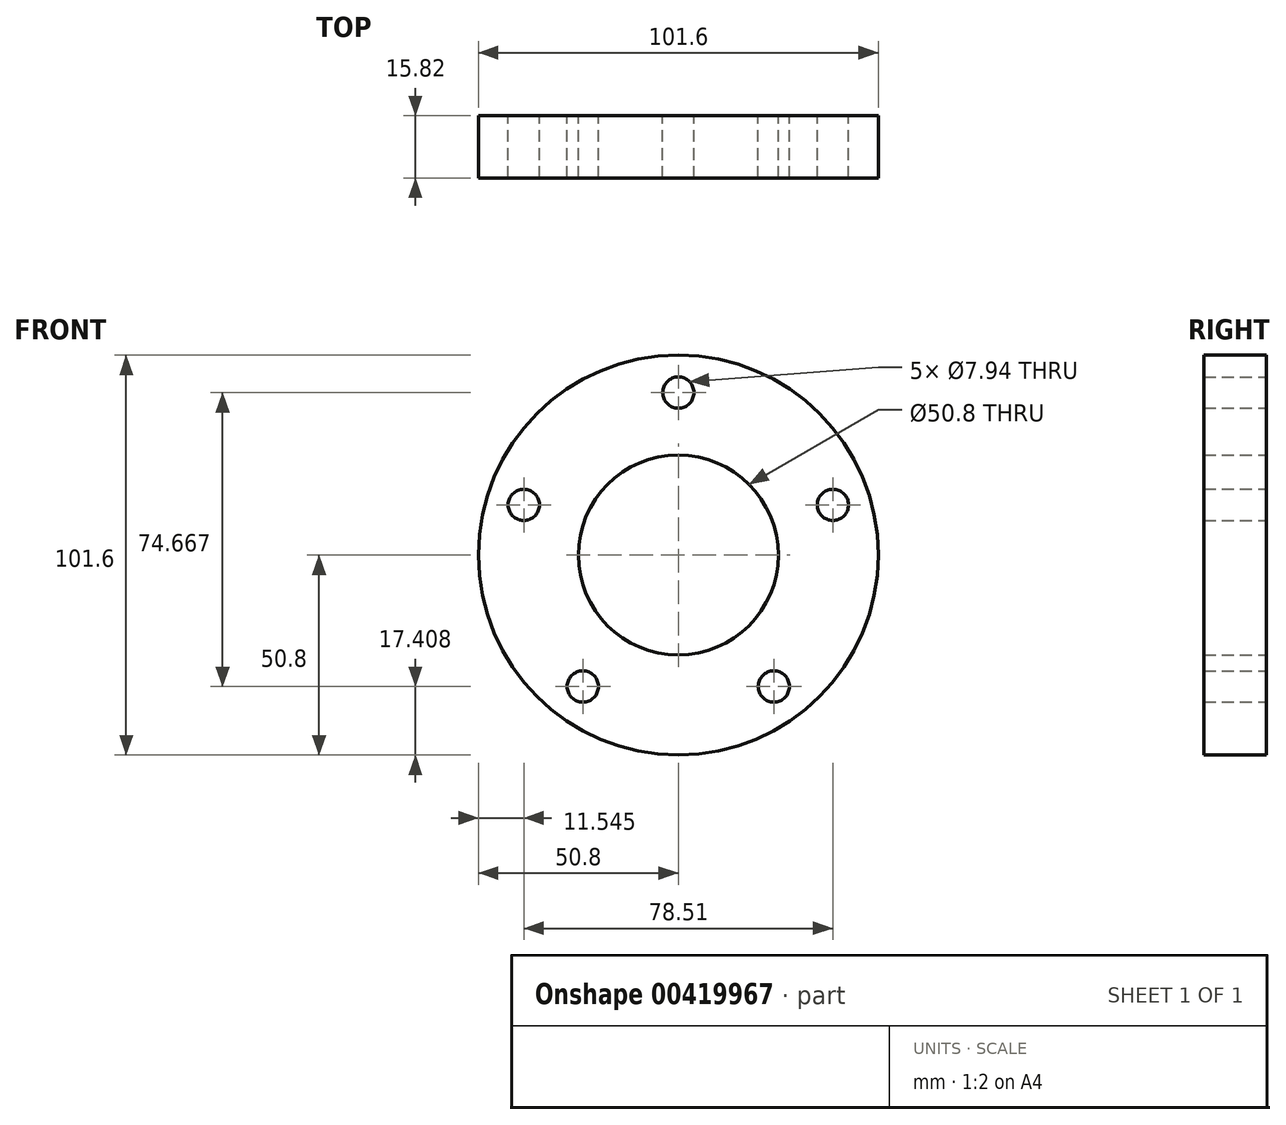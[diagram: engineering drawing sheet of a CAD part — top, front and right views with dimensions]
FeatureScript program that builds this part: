
annotation { "Feature Type Name" : "Feature", "Feature Type Description" : "" }
export const myFeature = defineFeature(function(context is Context, id is Id, definition is map)
    precondition{}
    {
        {
            var Q0;
            Q0=qCreatedBy(makeId("Front.planeOp"),FACE);
            var sketch = newSketch(context, id + "F0", { "sketchPlane" : qUnion([Q0])});
            skCircle(sketch, "E0", {"center": v(0, 0) * mm, "radius": 25.4 * mm});
            skCircle(sketch, "E1", {"center": v(0, 0) * mm, "radius": 50.8 * mm});
            skCircle(sketch, "E2", {"center": v(0, 0) * mm, "radius": 41.28 * mm});
            skLineSegment(sketch, "E3", {"start": v(0, 41.28) * mm, "end": v(0, 0) * mm});
            skLineSegment(sketch, "E4", {"start": v(0, 0) * mm, "end": v(39.25, 12.75) * mm});
            skLineSegment(sketch, "E5", {"start": v(0, 0) * mm, "end": v(24.26, -33.4) * mm});
            skLineSegment(sketch, "E6", {"start": v(0, 0) * mm, "end": v(-24.26, -33.4) * mm});
            skLineSegment(sketch, "E7", {"start": v(0, 0) * mm, "end": v(-39.25, 12.75) * mm});
            skPoint(sketch, "E8", {"position": v(0, 41.28) * mm});
            skPoint(sketch, "E9", {"position": v(-39.25, 12.75) * mm});
            skPoint(sketch, "E10", {"position": v(-24.26, -33.4) * mm});
            skPoint(sketch, "E11", {"position": v(24.26, -33.4) * mm});
            skPoint(sketch, "E12", {"position": v(39.25, 12.75) * mm});
            skSolve(sketch);
        }
        {
            var Q0;
            {var subQ0=sQuery(id+"F0.wireOp",EDGE,"E3");var subQ1=sQuery(id+"F0.wireOp",EDGE,"E0");var subQ2=makeQuery(id+"F0.imprint","INTERSECT",VERTEX,{"derivedFrom":[subQ1,subQ0]});Q0=makeQuery(id+"F0.imprint","IMPRINT",FACE,{"disambiguationData":[TD([[makeQuery(id+"F0.imprint","IMPRINT",EDGE,{"disambiguationData":[TD([[subQ2,1.0]])],"derivedFrom":subQ1}),-1.0]])]});}
            var Q1;
            Q1=makeQuery(id+"F0.imprint","IMPRINT",FACE,{"disambiguationData":[TD([[makeQuery(id+"F0.imprint","IMPRINT",EDGE,{"derivedFrom":sQuery(id+"F0.wireOp",EDGE,"E1")}),1.0]])]});
            var Q2;
            {var subQ0=sQuery(id+"F0.wireOp",EDGE,"E3");var subQ1=sQuery(id+"F0.wireOp",EDGE,"E0");var subQ2=makeQuery(id+"F0.imprint","INTERSECT",VERTEX,{"derivedFrom":[subQ1,subQ0]});Q2=makeQuery(id+"F0.imprint","IMPRINT",FACE,{"disambiguationData":[TD([[makeQuery(id+"F0.imprint","IMPRINT",EDGE,{"disambiguationData":[TD([[subQ2,-1.0]])],"derivedFrom":subQ1}),-1.0]])]});}
            var Q3;
            {var subQ0=sQuery(id+"F0.wireOp",EDGE,"E7");var subQ1=sQuery(id+"F0.wireOp",EDGE,"E0");var subQ2=makeQuery(id+"F0.imprint","INTERSECT",VERTEX,{"derivedFrom":[subQ1,subQ0]});Q3=makeQuery(id+"F0.imprint","IMPRINT",FACE,{"disambiguationData":[TD([[makeQuery(id+"F0.imprint","IMPRINT",EDGE,{"disambiguationData":[TD([[subQ2,-1.0]])],"derivedFrom":subQ1}),-1.0]])]});}
            var Q4;
            {var subQ0=sQuery(id+"F0.wireOp",EDGE,"E4");var subQ1=sQuery(id+"F0.wireOp",EDGE,"E0");var subQ2=makeQuery(id+"F0.imprint","INTERSECT",VERTEX,{"derivedFrom":[subQ1,subQ0]});Q4=makeQuery(id+"F0.imprint","IMPRINT",FACE,{"disambiguationData":[TD([[makeQuery(id+"F0.imprint","IMPRINT",EDGE,{"disambiguationData":[TD([[subQ2,1.0]])],"derivedFrom":subQ1}),-1.0]])]});}
            var Q5;
            {var subQ0=sQuery(id+"F0.wireOp",EDGE,"E6");var subQ1=sQuery(id+"F0.wireOp",EDGE,"E0");var subQ2=makeQuery(id+"F0.imprint","INTERSECT",VERTEX,{"derivedFrom":[subQ1,subQ0]});Q5=makeQuery(id+"F0.imprint","IMPRINT",FACE,{"disambiguationData":[TD([[makeQuery(id+"F0.imprint","IMPRINT",EDGE,{"disambiguationData":[TD([[subQ2,-1.0]])],"derivedFrom":subQ1}),-1.0]])]});}
            extrude(context, id + "F1", {"entities" : qUnion([Q0, Q1, Q2, Q3, Q4, Q5]), "endBound" : BoundingType.SYMMETRIC, "depth" : 15.82 * mm, "offsetDistance" : 25.4 * mm});
        }
        {
            var Q0;
            Q0=sQuery(id+"F0.wireOp",VERTEX,"E9");
            var Q1;
            Q1=sQuery(id+"F0.wireOp",VERTEX,"E8");
            var Q2;
            Q2=sQuery(id+"F0.wireOp",VERTEX,"E12");
            var Q3;
            Q3=sQuery(id+"F0.wireOp",VERTEX,"E11");
            var Q4;
            Q4=sQuery(id+"F0.wireOp",VERTEX,"E10");
            var Q5;
            Q5=makeQuery(id+"F1.opExtrude","SWEPT_BODY",BODY,{"disambiguationData":[OSD([sQuery(id+"F0.wireOp",EDGE,"E0"),sQuery(id+"F0.wireOp",EDGE,"E1")])]});
            hole(context, id + "F2", {"style" : HoleStyle.SIMPLE, "endStyle" : HoleEndStyle.THROUGH, "oppositeDirection" : true, "holeDiameter" : 7.94 * mm, "majorDiameter" : 6.35 * mm, "isTappedThrough" : true, "tappedDepth" : 12.7 * mm, "tapClearance" : 3, "locations" : qUnion([Q0, Q1, Q2, Q3, Q4]), "scope" : qUnion([Q5])});
        }
        {
            var Q0;
            Q0=sQuery(id+"F0.wireOp",VERTEX,"E8");
            var Q1;
            Q1=sQuery(id+"F0.wireOp",VERTEX,"E12");
            var Q2;
            Q2=sQuery(id+"F0.wireOp",VERTEX,"E11");
            var Q3;
            Q3=sQuery(id+"F0.wireOp",VERTEX,"E10");
            var Q4;
            Q4=sQuery(id+"F0.wireOp",VERTEX,"E9");
            var Q5;
            Q5=makeQuery(id+"F1.opExtrude","SWEPT_BODY",BODY,{"disambiguationData":[OSD([sQuery(id+"F0.wireOp",EDGE,"E0"),sQuery(id+"F0.wireOp",EDGE,"E1")])]});
            hole(context, id + "F3", {"style" : HoleStyle.SIMPLE, "endStyle" : HoleEndStyle.THROUGH, "holeDiameter" : 7.94 * mm, "majorDiameter" : 6.35 * mm, "isTappedThrough" : true, "tappedDepth" : 12.7 * mm, "tapClearance" : 3, "locations" : qUnion([Q0, Q1, Q2, Q3, Q4]), "scope" : qUnion([Q5])});
        }
    });
